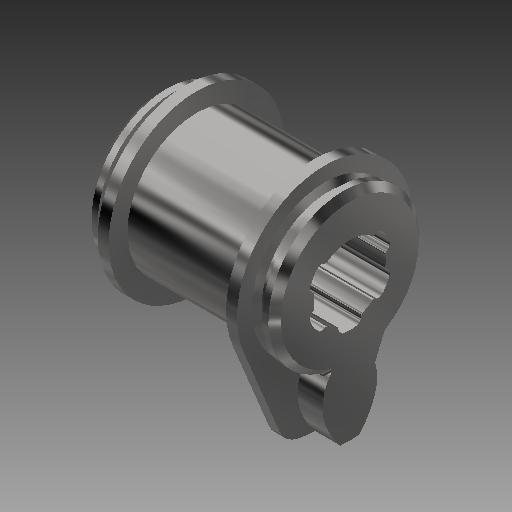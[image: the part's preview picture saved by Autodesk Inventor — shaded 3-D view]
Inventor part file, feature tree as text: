
AUTODESK INVENTOR PART (.ipt)
format: ipt  version: 2019 (Build 230136000, 136)  size: 398,848 bytes
history: native  units: mm
features: chamfer x3, sketch x3, extrude x3, revolve x1, fillet x1, plane x1
ambient origin geometry x8: Origin, YZ Plane, XZ Plane, XY Plane, X Axis, Y Axis, Z Axis, Center Point
bodies: Solid1 (feature_tree)
feature tree (12):
  revolve  "Revolution1"  [1 undecoded]
  chamfer  "Chamfer1"  Distance=14.049998mm
  chamfer  "Chamfer2"  Distance=1.3mm
  chamfer  "Chamfer3"  Distance=1.5mm
  sketch  "Sketch2"  dims[d2=1.5mm]
  extrude  "Extrusion1"  Depth=22.65mm
  extrude  "Extrusion2"  Depth=22.65mm
  fillet  "Fillet1"  Radius=10.5mm
  plane  "Work Plane1"
  extrude  "Extrusion3"  Depth=22.65mm
  sketch  "Sketch1"  dims[d0=9.0mm d1=1.5mm]
  sketch  "Sketch4"  dims[d3=1.300002mm d4=14.049998mm d5=1.3mm d6=1.5mm d7=22.65mm d8=8.0mm d9=10.5mm d10=8.25mm d11=10.5mm d12=8.0mm d13=9.0mm d14=90.0deg d15=0.75mm d16=2.0mm d17=45.0deg d18=0.75mm d19=2.0mm d20=30.0deg d21=0.75mm d22=2.0mm d23=30.0deg d24=33.0mm d25=22.5deg d26=22.5deg d27=3.0mm d28=5.998437mm d29=5.998437mm d30=10.185951mm d31=10.185951mm d32=19.0mm d33=19.0mm d34=10.5mm d35=11.557483mm d36=8.0mm d37=5.25mm d38=5.25mm d39=9.5mm d40=9.5mm d41=3.0mm d42=0.0mm d43=1.300003mm d44=0.0mm d45=0.25mm d46=1.300003mm d47=0.0mm]
note: 1 required parameter value undecoded (feature->parameter linkage not recoverable at this tier; creation-order binding heuristic only, values carry confidence <= 0.55)
